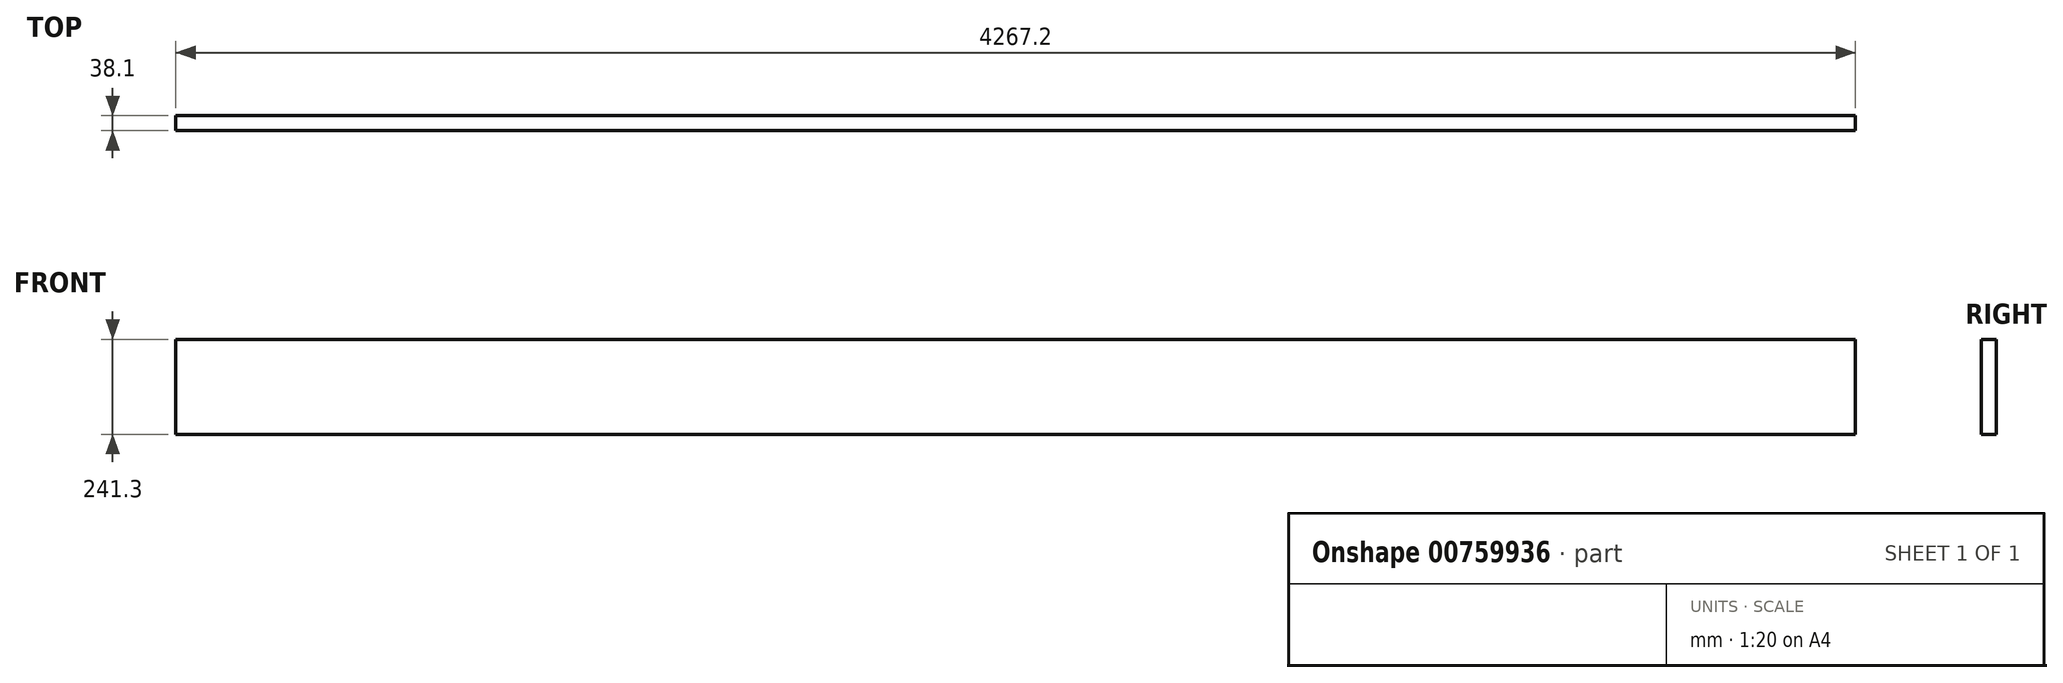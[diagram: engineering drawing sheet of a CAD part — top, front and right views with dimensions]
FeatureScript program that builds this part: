
annotation { "Feature Type Name" : "Feature", "Feature Type Description" : "" }
export const myFeature = defineFeature(function(context is Context, id is Id, definition is map)
    precondition{}
    {
        {
            var Q0;
            Q0=qCreatedBy(makeId("Front.planeOp"),FACE);
            var sketch = newSketch(context, id + "F0", { "sketchPlane" : qUnion([Q0])});
            skLineSegment(sketch, "E0.bottom", {"start": v(-2133.6, 120.65) * mm, "end": v(2133.6, 120.65) * mm});
            skLineSegment(sketch, "E0.top", {"start": v(-2133.6, -120.65) * mm, "end": v(2133.6, -120.65) * mm});
            skLineSegment(sketch, "E0.left", {"start": v(-2133.6, 120.65) * mm, "end": v(-2133.6, -120.65) * mm});
            skLineSegment(sketch, "E0.right", {"start": v(2133.6, 120.65) * mm, "end": v(2133.6, -120.65) * mm});
            skPoint(sketch, "E0.middle", {"position": v(0, 0) * mm});
            skSolve(sketch);
        }
        {
            var Q0;
            Q0 = qSketchRegion(id + "F0", true);
            extrude(context, id + "F1", {"entities" : qUnion([Q0]), "endBound" : BoundingType.SYMMETRIC, "depth" : 38.1 * mm, "offsetDistance" : 25.4 * mm});
        }
        {
            var Q0;
            Q0=makeQuery(id+"F1.opExtrude","SWEPT_BODY",BODY,{"disambiguationData":[OSD([sQuery(id+"F0.wireOp",EDGE,"E0.bottom"),sQuery(id+"F0.wireOp",EDGE,"E0.top"),sQuery(id+"F0.wireOp",EDGE,"E0.left"),sQuery(id+"F0.wireOp",EDGE,"E0.right")])]});
            transform(context, id + "F2", {"entities" : qUnion([Q0]), "transformType" : TransformType.TRANSLATION_3D, "dx" : 0 * mm, "dy" : 0 * mm, "dz" : 0 * mm, "makeCopy" : true});
        }
        {
            var Q0;
            Q0=makeQuery(id+"F2.opPattern","COPY",BODY,{"derivedFrom":makeQuery(id+"F1.opExtrude","SWEPT_BODY",BODY,{"disambiguationData":[OSD([sQuery(id+"F0.wireOp",EDGE,"E0.bottom"),sQuery(id+"F0.wireOp",EDGE,"E0.top"),sQuery(id+"F0.wireOp",EDGE,"E0.left"),sQuery(id+"F0.wireOp",EDGE,"E0.right")])]}),"instanceName":"1"});
            deleteBodies(context, id + "F3", {"entities" : qUnion([Q0])});
        }
    });
